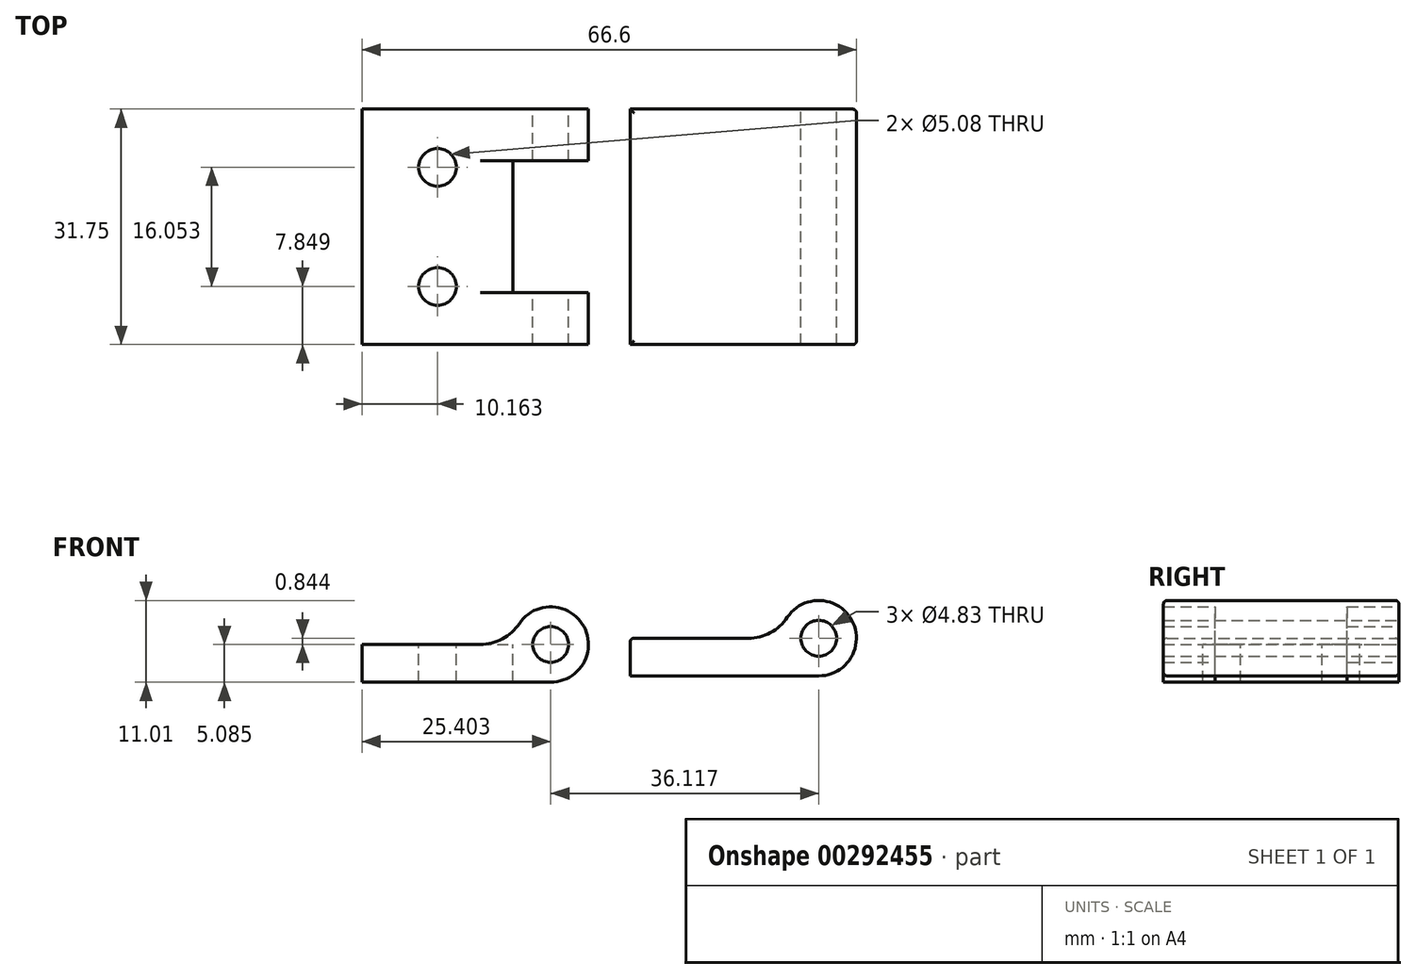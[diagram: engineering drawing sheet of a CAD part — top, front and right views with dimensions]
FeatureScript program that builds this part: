
annotation { "Feature Type Name" : "Feature", "Feature Type Description" : "" }
export const myFeature = defineFeature(function(context is Context, id is Id, definition is map)
    precondition{}
    {
        {
            var Q0;
            Q0=qCreatedBy(makeId("Front.planeOp"),FACE);
            var sketch = newSketch(context, id + "F0", { "sketchPlane" : qUnion([Q0])});
            skLineSegment(sketch, "E0.bottom", {"start": v(-61.52, 5.75) * mm, "end": v(-41.2, 5.75) * mm});
            skLineSegment(sketch, "E0.top", {"start": v(-61.52, 0.67) * mm, "end": v(-36.12, 0.67) * mm});
            skLineSegment(sketch, "E0.left", {"start": v(-61.52, 5.75) * mm, "end": v(-61.52, 0.67) * mm});
            skArc(sketch, "E1", {"start": v(-36.12, 0.67) * mm, "mid": v(-32.53, 9.35) * mm, "end": v(-41.2, 5.75) * mm});
            skCircle(sketch, "E2", {"center": v(-36.12, 5.75) * mm, "radius": 2.41 * mm});
            skLineSegment(sketch, "E3.bottom", {"start": v(-25.4, 6.6) * mm, "end": v(-5.08, 6.6) * mm});
            skLineSegment(sketch, "E3.top", {"start": v(-25.4, 1.52) * mm, "end": v(0, 1.52) * mm});
            skLineSegment(sketch, "E3.left", {"start": v(-25.4, 6.6) * mm, "end": v(-25.4, 1.52) * mm});
            skArc(sketch, "E4", {"start": v(0, 1.52) * mm, "mid": v(3.6, 10.2) * mm, "end": v(-5.08, 6.6) * mm});
            skCircle(sketch, "E5", {"center": v(0, 6.6) * mm, "radius": 2.41 * mm});
            skSolve(sketch);
        }
        {
            var Q0;
            Q0 = qSketchRegion(id + "F0", true);
            extrude(context, id + "F1", {"entities" : qUnion([Q0]), "depth" : 31.75 * mm});
        }
        {
            var Q0;
            Q0=makeQuery(id+"F1.opExtrude","SWEPT_FACE",FACE,{"disambiguationData":[OSD([sQuery(id+"F0.wireOp",EDGE,"E0.bottom")])]});
            var sketch = newSketch(context, id + "F2", { "sketchPlane" : qUnion([Q0])});
            skLineSegment(sketch, "E6.bottom", {"start": v(-41.2, -6.99) * mm, "end": v(-31.04, -6.99) * mm});
            skLineSegment(sketch, "E6.top", {"start": v(-41.2, -24.77) * mm, "end": v(-31.04, -24.77) * mm});
            skLineSegment(sketch, "E6.left", {"start": v(-41.2, -6.99) * mm, "end": v(-41.2, -24.77) * mm});
            skLineSegment(sketch, "E6.right", {"start": v(-31.04, -6.99) * mm, "end": v(-31.04, -24.77) * mm});
            skLineSegment(sketch, "E7.0", {"start": v(-31.04, 0) * mm, "end": v(-41.2, 0) * mm});
            skLineSegment(sketch, "E8.0", {"start": v(-31.04, -31.75) * mm, "end": v(-41.2, -31.75) * mm});
            skLineSegment(sketch, "E9", {"start": v(-36.12, -24.77) * mm, "end": v(-36.12, -31.75) * mm, "construction": true});
            skLineSegment(sketch, "E10", {"start": v(-36.12, -6.99) * mm, "end": v(-36.12, 0) * mm, "construction": true});
            skSolve(sketch);
        }
        {
            var Q0;
            Q0 = qSketchRegion(id + "F2", true);
            var Q1;
            Q1=makeQuery(id+"F1.opExtrude","SWEPT_FACE",FACE,{"disambiguationData":[OSD([sQuery(id+"F0.wireOp",EDGE,"E0.top")])]});
            var Q2;
            Q2=makeQuery(id+"F1.opExtrude","SWEPT_FACE",FACE,{"disambiguationData":[OSD([sQuery(id+"F0.wireOp",EDGE,"E1")])]});
            extrude(context, id + "F3", {"entities" : qUnion([Q0]), "operationType" : NewBodyOperationType.REMOVE, "endBound" : BoundingType.UP_TO_SURFACE, "oppositeDirection" : true, "endBoundEntityFace" : qUnion([Q1]), "depth" : 25.4 * mm, "hasSecondDirection" : true, "secondDirectionBound" : SecondDirectionBoundingType.UP_TO_SURFACE, "secondDirectionOppositeDirection" : false, "secondDirectionBoundEntityFace" : qUnion([Q2]), "secondDirectionDepth" : 25.4 * mm});
        }
        {
            var Q0;
            Q0=makeQuery(id+"F1.opExtrude","SWEPT_FACE",FACE,{"disambiguationData":[OSD([sQuery(id+"F0.wireOp",EDGE,"E0.bottom")])]});
            var sketch = newSketch(context, id + "F4", { "sketchPlane" : qUnion([Q0])});
            skCircle(sketch, "E11", {"center": v(-51.36, -7.85) * mm, "radius": 2.54 * mm});
            skPoint(sketch, "E11.centerSnap0", {"position": v(-51.36, 0) * mm});
            skCircle(sketch, "E12", {"center": v(-51.36, -23.9) * mm, "radius": 2.54 * mm});
            skPoint(sketch, "E12.centerSnap0", {"position": v(-51.36, -31.75) * mm});
            skLineSegment(sketch, "E13", {"start": v(-51.36, -23.9) * mm, "end": v(-51.36, -31.75) * mm, "construction": true});
            skLineSegment(sketch, "E14", {"start": v(-51.36, 0) * mm, "end": v(-51.36, -7.85) * mm, "construction": true});
            skSolve(sketch);
        }
        {
            var Q0;
            Q0 = qSketchRegion(id + "F4", true);
            var Q1;
            Q1=makeQuery(id+"F1.opExtrude","SWEPT_FACE",FACE,{"disambiguationData":[OSD([sQuery(id+"F0.wireOp",EDGE,"E0.top")])]});
            extrude(context, id + "F5", {"entities" : qUnion([Q0]), "operationType" : NewBodyOperationType.REMOVE, "endBound" : BoundingType.UP_TO_SURFACE, "oppositeDirection" : true, "endBoundEntityFace" : qUnion([Q1]), "depth" : 25.4 * mm});
        }
        {
            var Q0;
            {var subQ0=sQuery(id+"F0.wireOp",EDGE,"E1");var subQ1=sQuery(id+"F0.wireOp",EDGE,"E0.bottom");Q0=makeQuery(id+"F3.boolean.opBoolean","SPLIT",EDGE,{"disambiguationData":[TD([makeQuery(id+"F3.opExtrude","SWEPT_FACE",FACE,{"disambiguationData":[OSD([sQuery(id+"F2.wireOp",EDGE,"E6.bottom")])]})])],"derivedFrom":makeQuery(id+"F1.opExtrude","SWEPT_EDGE",EDGE,{"disambiguationData":[OSD([subQ1,subQ0])]})});}
            var Q1;
            {var subQ0=sQuery(id+"F0.wireOp",EDGE,"E1");var subQ1=sQuery(id+"F0.wireOp",EDGE,"E0.bottom");Q1=makeQuery(id+"F3.boolean.opBoolean","SPLIT",EDGE,{"disambiguationData":[TD([makeQuery(id+"F3.opExtrude","SWEPT_FACE",FACE,{"disambiguationData":[OSD([sQuery(id+"F2.wireOp",EDGE,"E6.top")])]})])],"derivedFrom":makeQuery(id+"F1.opExtrude","SWEPT_EDGE",EDGE,{"disambiguationData":[OSD([subQ1,subQ0])]})});}
            var Q2;
            Q2=makeQuery(id+"F1.opExtrude","SWEPT_EDGE",EDGE,{"disambiguationData":[OSD([sQuery(id+"F0.wireOp",EDGE,"E3.bottom"),sQuery(id+"F0.wireOp",EDGE,"E4")])]});
            fillet(context, id + "F6", {"entities" : qUnion([Q0, Q1, Q2]), "radius" : 6.35 * mm, "tangentPropagation" : true, "allowEdgeOverflow" : false});
        }
        {
            var Q0;
            Q0=makeQuery(id+"F1.opExtrude","CAP_EDGE",EDGE,{"disambiguationData":[OSD([sQuery(id+"F0.wireOp",EDGE,"E3.bottom")])],"isStart":false});
            var Q1;
            Q1=makeQuery(id+"F1.opExtrude","CAP_EDGE",EDGE,{"disambiguationData":[OSD([sQuery(id+"F0.wireOp",EDGE,"E3.bottom")])],"isStart":true});
            var Q2;
            Q2=makeQuery(id+"F1.opExtrude","SWEPT_EDGE",EDGE,{"disambiguationData":[OSD([sQuery(id+"F0.wireOp",EDGE,"E3.bottom"),sQuery(id+"F0.wireOp",EDGE,"E3.left")])]});
            fillet(context, id + "F7", {"entities" : qUnion([Q0, Q1, Q2]), "radius" : 0.5 * mm, "tangentPropagation" : true, "allowEdgeOverflow" : false});
        }
    });
